# Revit family: DBLTD_TheSenatorGroup_OfficeTables_Colab_Stackable
name_source: partatom
category: Furniture
units: mm (PartAtom-declared; Revit-internal decimal feet)

## family parameters
Always vertical = Yes
Cut with Voids When Loaded = No
OmniClass Number = 23.40.20.00
OmniClass Title = General Furniture and Specialties
Room Calculation Point = No
Shared = Yes
Work Plane-Based = No

## types (1)
- 740mm H x 840mm W x 550mm D
    Assembly Code = E2020200
    AssetType = Movable
    Category = Pr_40_50_21_60 Office tables
    Color = Frame; Honey Yellow | Forest Green | Smoke Grey | Ocean Blue. Top; UM Urban Maple | WH White | WK Winter Oak | SO Strata Oak | LY Clay | CW Carini Walnut | AT Autumn | BH Beech | HD Highland Oak | DN Denim | LG Light Grey
    Constituents = Frame, Top
    Cost = 0 $
    Default Elevation = 0 mm  [stored 0 ft]
    Description = 740mm H x 840mm W x 550mm D
    DurationUnit = years
    ExpectedLife = 5
    Features = Stacking Table stacks 5no high
    Finish = Frame; Honey Yellow | Forest Green | Smoke Grey | Ocean Blue. Top; UM Urban Maple | WH White | WK Winter Oak | SO Strata Oak | LY Clay | CW Carini Walnut | AT Autumn | BH Beech | HD Highland Oak | DN Denim | LG Light Grey
    Keynote = Pr_40_50_21_60 Office tables
    Manufacturer = The Senator Group
    ManufacturerName = The Senator Group
    ManufacturerURL = https://www.thesenatorgroup.com
    Material = Frame: Metal. Top: 25mm MFC
    Model = CBSTK
    ModelNumber = CBSTK
    ModelReference = 740mm H x 840mm W x 550mm D
    Name = Table
    NominalDepth = 550 mm  [stored 1.80446 ft]
    NominalWidth = 840 mm  [stored 2.75591 ft]
    NumberOfChairs = 0
    ProductInformation = https://www.senator.online
    Shape = Rectangular
    Size = 740 x 840 x 550 mm
    Type Comments = 740mm H x 840mm W x 550mm D
    URL = https://www.thesenatorgroup.com
    Uniclass2015Code = Pr_40_50_21_60
    Uniclass2015Title = Office tables
    Uniclass2015Version = Products v1.15
    Version = 1
    WarrantyDescription = The Senator Group warrants that its manufactured products are free from manufacturing defects - in materials or workmanship - for a period of five (5) years.
Allermuir will repair, or replace (at Allermuir’s sole discretion) with comparable free of charge materials/ components, any product/ component which fails under normal use in a single shift environment, as a result of a defect in the materials and/or workmanship.

Exceptions -
Non-standard product - 2 years
Screen-mounted Accessories/ Dry-wipe Boards - 2 years
Electrical and/or electronic componentry - 2 years

Exclusions - Allermuir does not warrant:
Failure due to normal “Wear and Tear”.
Natural variations in appearance of wood - its grain, figure and colour.
Changes in surface appearance resulting from exposure to light, and the natural ageing process of wood.
Changes in surface appearance resulting from the misuse of cleaning materials and methods/ damage form sharp objects/ imprinting from writing implements.
Natural variations in Leather - its marks, scars and wrinkles.
Product stored/ exposed to extreme operational conditions.
Consumable components such as Fuses/ Lights/ lamps/ transformers/etc.
Other Manufacturer’s product supplied by Allermuir (their own warranty shall apply where possible).
Non-standard fabrics/ finishes or veneers used. Allermuir only checks the manufacturing quality of Customer’s
Own Material (COM) and provides no warranty for the finish/ fabric itself.
Product which has not been installed/ moved/ reconfigured by Allermuir approved personnel.
Allermuir shall be under no liability whatsoever for any consequential damage, loss or other expenses whether arising out of contract, negligence or otherwise.
    WarrantyDurationLabor = 5
    WarrantyDurationParts = 5
    WarrantyDurationUnit = years
    WarrantyGuarantorLabor = https://www.thesenatorgroup.com
    WarrantyGuarantorParts = https://www.thesenatorgroup.com
    WorksurfaceArea = 0.46 m²
    WorktopMaterial = DBLTD_TheSenatorGroup_Wood_LightGrey

note: [stored X ft] marks values corroborated as IEEE doubles in the binary element streams (Revit-internal decimal feet)

## geometry (parser evidence)
native form markers: Sweep x3
no freeform markers — native parametric forms only
